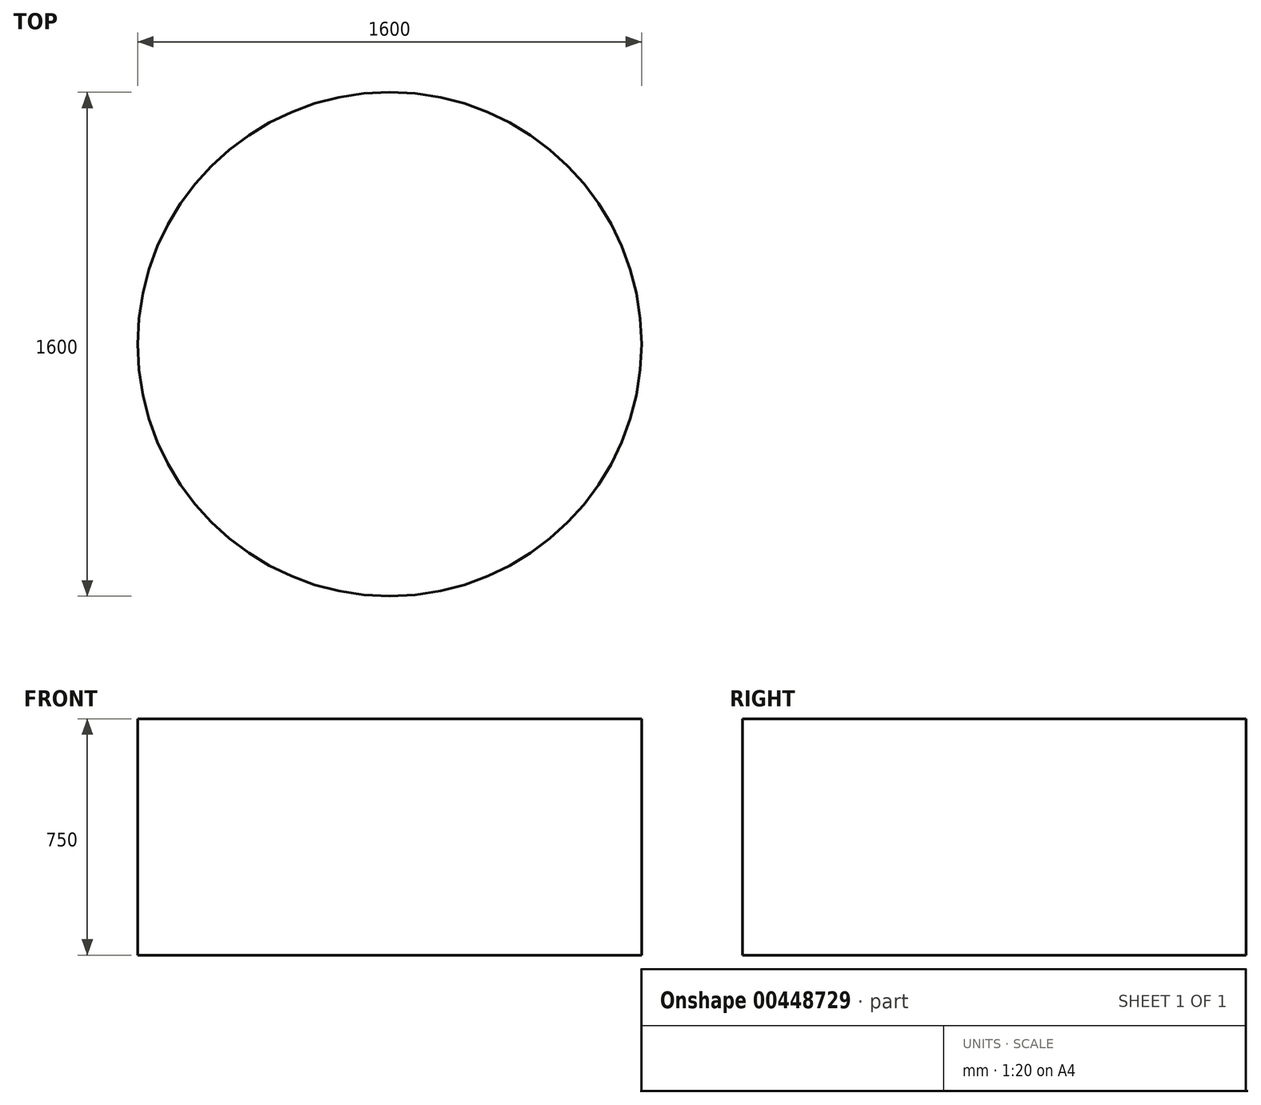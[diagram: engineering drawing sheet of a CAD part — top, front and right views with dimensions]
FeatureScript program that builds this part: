
annotation { "Feature Type Name" : "Feature", "Feature Type Description" : "" }
export const myFeature = defineFeature(function(context is Context, id is Id, definition is map)
    precondition{}
    {
        {
            var Q0;
            Q0=qCreatedBy(makeId("Top.planeOp"),FACE);
            var sketch = newSketch(context, id + "F0", { "sketchPlane" : qUnion([Q0])});
            skCircle(sketch, "E0", {"center": v(0, 0) * mm, "radius": 800 * mm});
            skSolve(sketch);
        }
        {
            var Q0;
            Q0=makeQuery(id+"F0.imprint","IMPRINT",FACE,{"disambiguationData":[TD([[makeQuery(id+"F0.imprint","IMPRINT",EDGE,{"derivedFrom":sQuery(id+"F0.wireOp",EDGE,"E0")}),1.0]])]});
            extrude(context, id + "F1", {"entities" : qUnion([Q0]), "depth" : 750 * mm, "offsetDistance" : 25 * mm});
        }
    });
